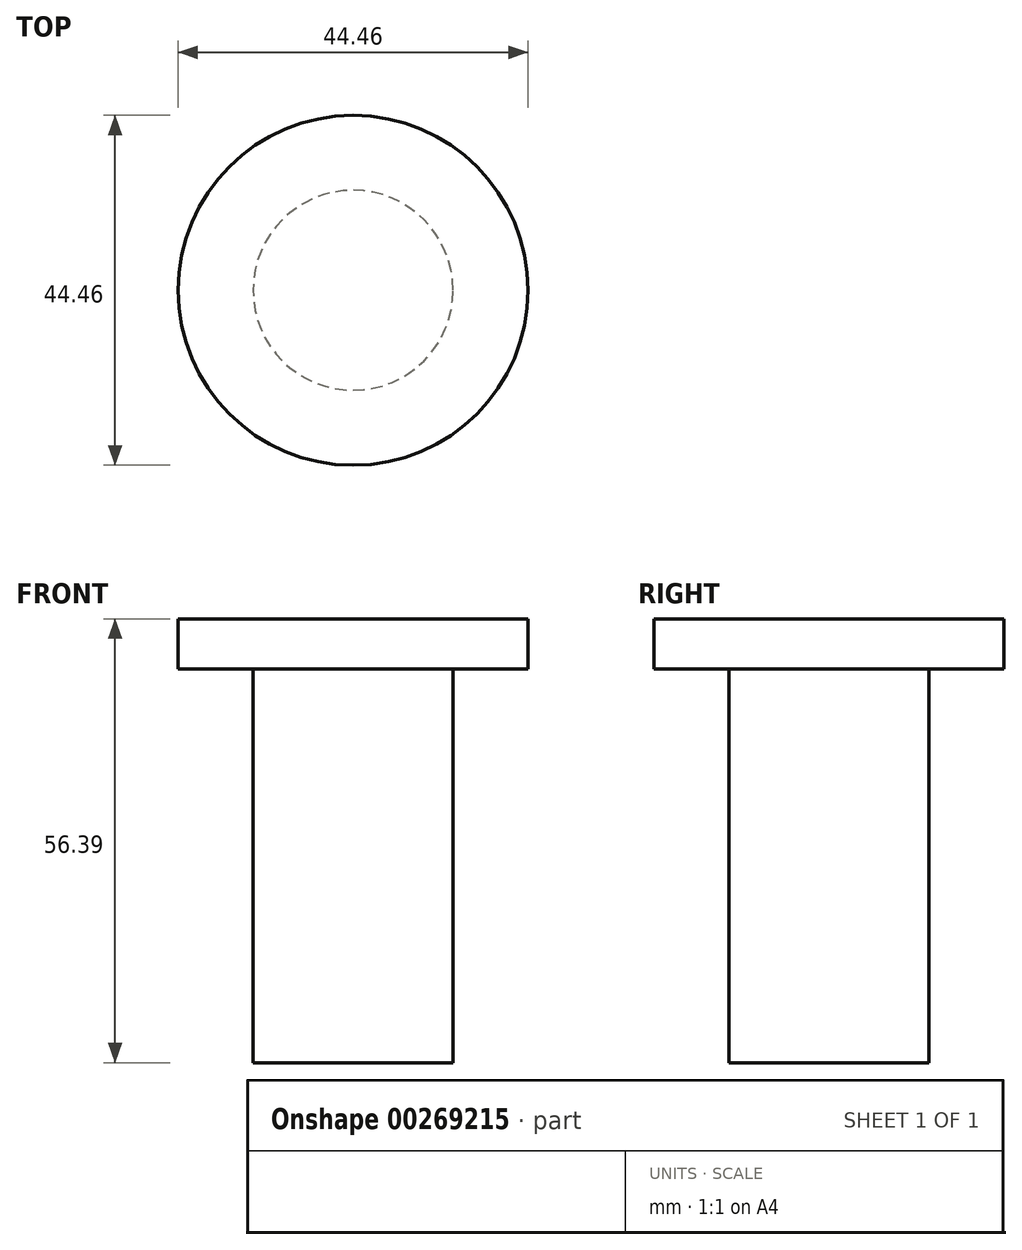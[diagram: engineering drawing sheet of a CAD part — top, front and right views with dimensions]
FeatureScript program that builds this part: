
annotation { "Feature Type Name" : "Feature", "Feature Type Description" : "" }
export const myFeature = defineFeature(function(context is Context, id is Id, definition is map)
    precondition{}
    {
        {
            var Q0;
            Q0=qCreatedBy(makeId("Top.planeOp"),FACE);
            var sketch = newSketch(context, id + "F0", { "sketchPlane" : qUnion([Q0])});
            skCircle(sketch, "E0", {"center": v(0, 0) * mm, "radius": 12.7 * mm});
            skSolve(sketch);
        }
        {
            var Q0;
            Q0=qSketchRegion(id+"F0",true);
            extrude(context, id + "F1", {"entities" : qUnion([Q0]), "depth" : 50.8 * mm});
        }
        {
            var Q0;
            Q0=qCreatedBy(makeId("Top.planeOp"),FACE);
            cPlane(context, id + "F2", {"entities" : qUnion([Q0]), "cplaneType" : CPlaneType.OFFSET, "offset" : 50.04 * mm, "width" : 152.4 * mm, "height" : 152.4 * mm});
        }
        {
            var Q0;
            Q0=qCreatedBy(id+"F2.planeOp",FACE);
            var sketch = newSketch(context, id + "F3", { "sketchPlane" : qUnion([Q0])});
            skCircle(sketch, "E1", {"center": v(0, 0) * mm, "radius": 22.23 * mm});
            skSolve(sketch);
        }
        {
            var Q0;
            Q0=qSketchRegion(id+"F3",true);
            extrude(context, id + "F4", {"entities" : qUnion([Q0]), "operationType" : NewBodyOperationType.ADD, "depth" : 6.35 * mm});
        }
    });
